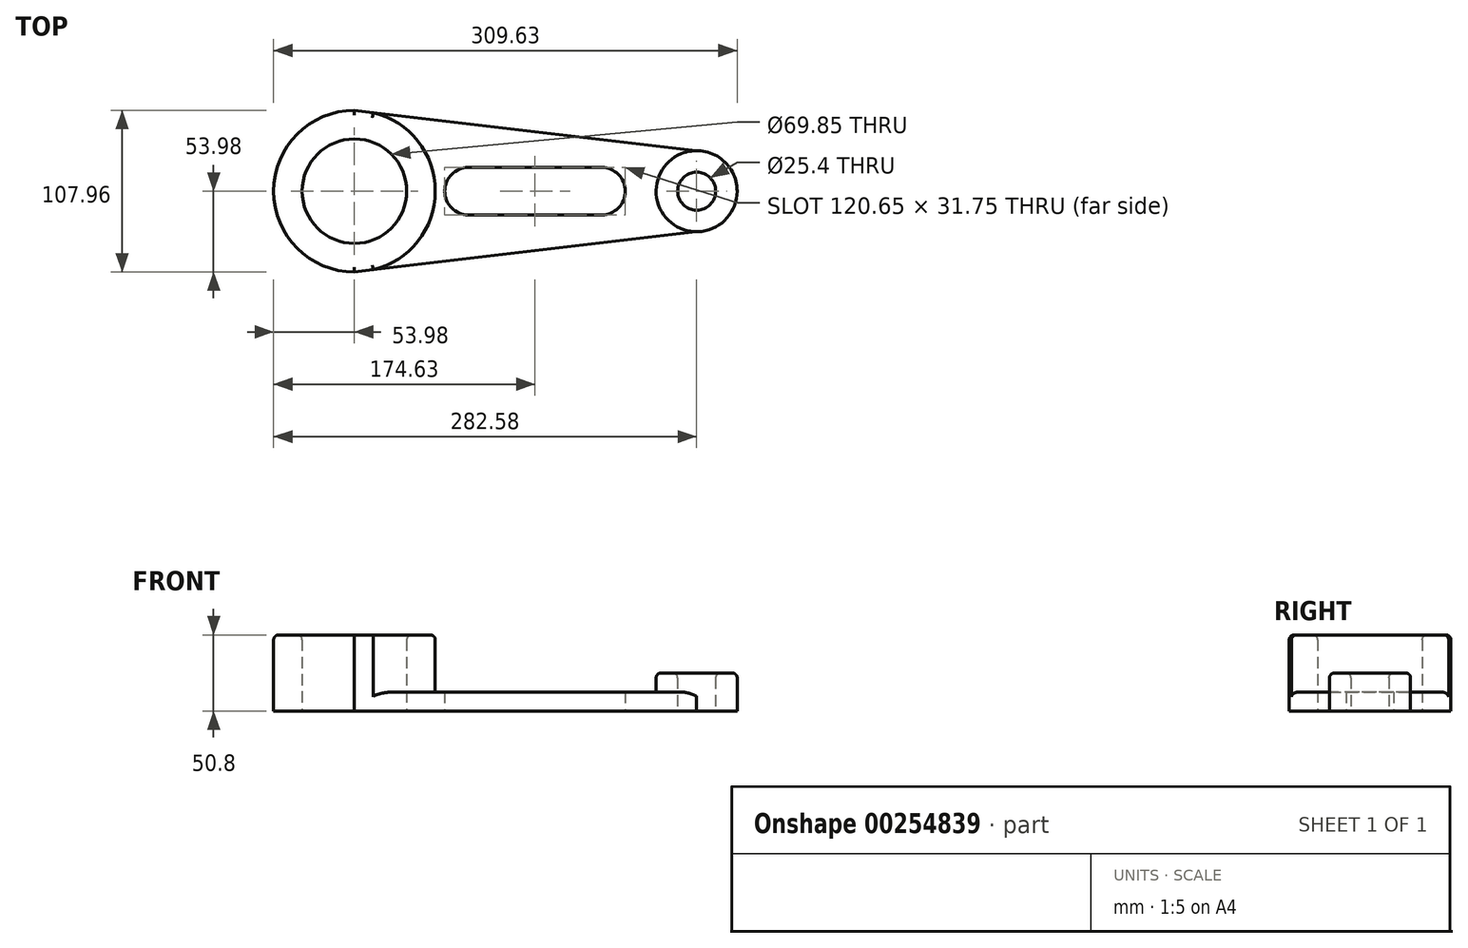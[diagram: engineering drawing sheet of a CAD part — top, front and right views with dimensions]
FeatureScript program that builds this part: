
annotation { "Feature Type Name" : "Feature", "Feature Type Description" : "" }
export const myFeature = defineFeature(function(context is Context, id is Id, definition is map)
    precondition{}
    {
        {
            var Q0;
            Q0=qCreatedBy(makeId("Top.planeOp"),FACE);
            var sketch = newSketch(context, id + "F0", { "sketchPlane" : qUnion([Q0])});
            skArc(sketch, "E0", {"start": v(0, 15.88) * mm, "mid": v(-15.88, 0) * mm, "end": v(0, -15.88) * mm});
            skArc(sketch, "E1", {"start": v(88.9, -15.88) * mm, "mid": v(104.78, 0) * mm, "end": v(88.9, 15.88) * mm});
            skLineSegment(sketch, "E2", {"start": v(0, 15.88) * mm, "end": v(88.9, 15.88) * mm});
            skLineSegment(sketch, "E3", {"start": v(88.9, -15.88) * mm, "end": v(0, -15.88) * mm});
            skCircle(sketch, "E4", {"center": v(-76.2, 0) * mm, "radius": 34.93 * mm});
            skCircle(sketch, "E5", {"center": v(-76.2, 0) * mm, "radius": 53.98 * mm});
            skCircle(sketch, "E6", {"center": v(152.4, 0) * mm, "radius": 12.7 * mm});
            skCircle(sketch, "E7", {"center": v(152.4, 0) * mm, "radius": 27.05 * mm});
            skLineSegment(sketch, "E8", {"start": v(152.4, -27.05) * mm, "end": v(-76.2, -53.97) * mm});
            skLineSegment(sketch, "E9", {"start": v(-76.2, 53.97) * mm, "end": v(152.4, 27.05) * mm});
            skSolve(sketch);
        }
        {
            var Q0;
            Q0=makeQuery(id+"F0.imprint","IMPRINT",FACE,{"disambiguationData":[TD([[makeQuery(id+"F0.imprint","IMPRINT",EDGE,{"derivedFrom":sQuery(id+"F0.wireOp",EDGE,"E4")}),-1.0]])]});
            extrude(context, id + "F1", {"entities" : qUnion([Q0]), "depth" : 50.8 * mm});
        }
        {
            var Q0;
            Q0=makeQuery(id+"F0.imprint","IMPRINT",FACE,{"disambiguationData":[TD([[makeQuery(id+"F0.imprint","IMPRINT",EDGE,{"derivedFrom":sQuery(id+"F0.wireOp",EDGE,"E0")}),-1.0]])]});
            extrude(context, id + "F2", {"entities" : qUnion([Q0]), "operationType" : NewBodyOperationType.ADD, "depth" : 12.7 * mm});
        }
        {
            var Q0;
            Q0=makeQuery(id+"F0.imprint","IMPRINT",FACE,{"disambiguationData":[TD([[makeQuery(id+"F0.imprint","IMPRINT",EDGE,{"derivedFrom":sQuery(id+"F0.wireOp",EDGE,"E6")}),-1.0]])]});
            extrude(context, id + "F3", {"entities" : qUnion([Q0]), "operationType" : NewBodyOperationType.ADD, "depth" : 25.4 * mm});
        }
        {
            var Q0;
            Q0=makeQuery(id+"F2.opExtrude","CAP_EDGE",EDGE,{"disambiguationData":[OSD([sQuery(id+"F0.wireOp",EDGE,"E9")])],"isStart":false});
            var Q1;
            Q1=makeQuery(id+"F2.opExtrude","CAP_EDGE",EDGE,{"disambiguationData":[OSD([sQuery(id+"F0.wireOp",EDGE,"E8")])],"isStart":false});
            var Q2;
            Q2=makeQuery(id+"F1.opExtrude","CAP_FACE",FACE,{"disambiguationData":[OSD([sQuery(id+"F0.wireOp",EDGE,"E4"),sQuery(id+"F0.wireOp",EDGE,"E5"),sQuery(id+"F0.wireOp",EDGE,"E8"),sQuery(id+"F0.wireOp",EDGE,"E9")])],"isStart":false});
            var Q3;
            Q3=makeQuery(id+"F3.opExtrude","CAP_FACE",FACE,{"disambiguationData":[OSD([sQuery(id+"F0.wireOp",EDGE,"E6"),sQuery(id+"F0.wireOp",EDGE,"E7")])],"isStart":false});
            fillet(context, id + "F4", {"entities" : qUnion([Q0, Q1, Q2, Q3]), "radius" : 3.17 * mm, "tangentPropagation" : true, "allowEdgeOverflow" : false});
        }
    });
